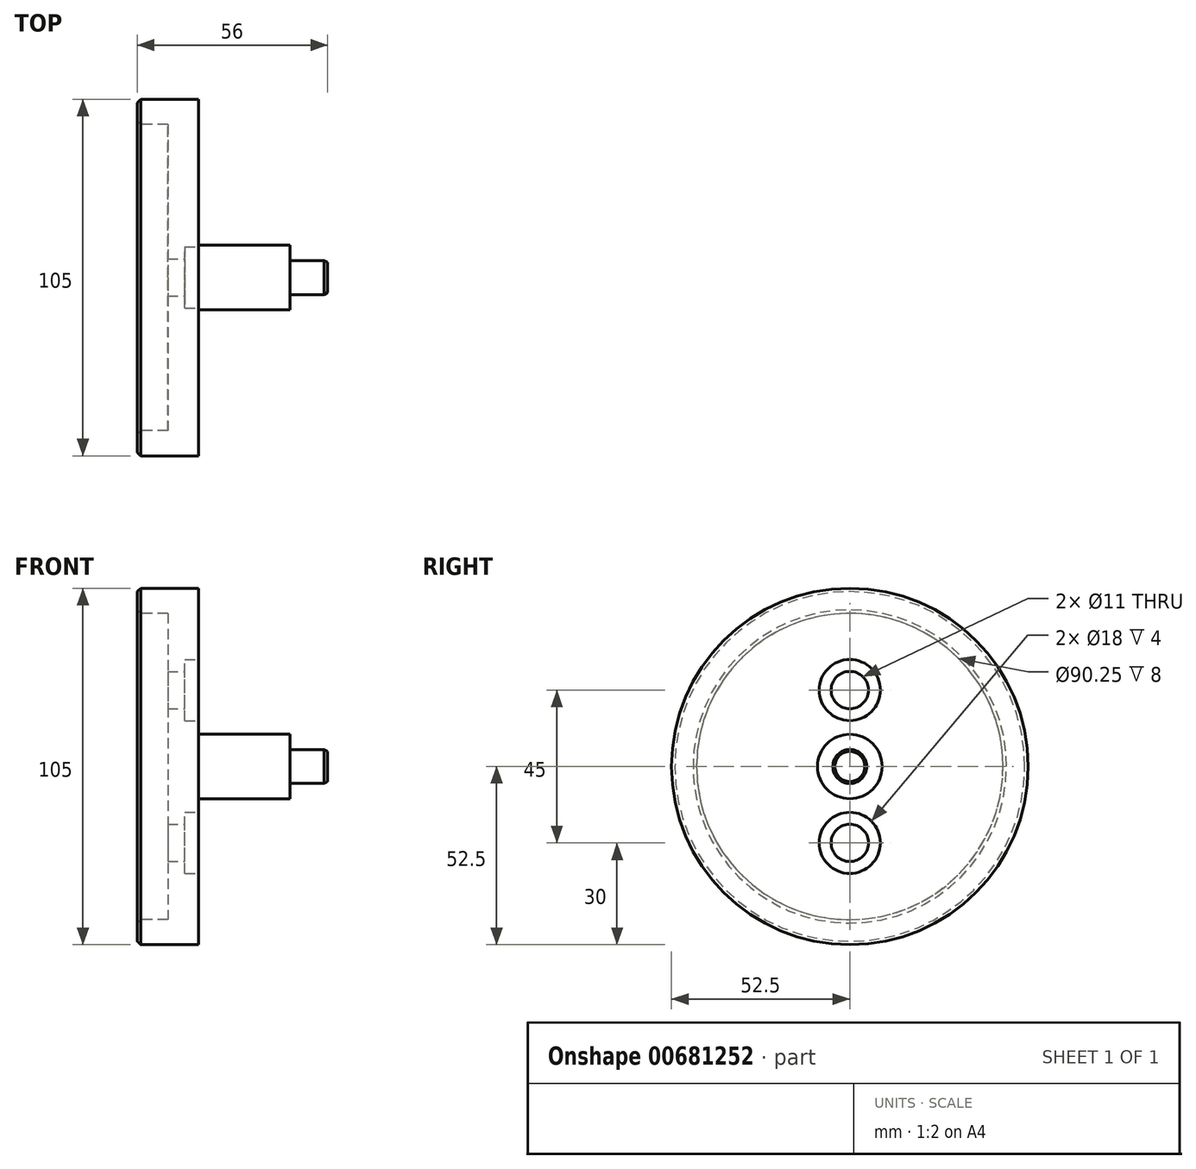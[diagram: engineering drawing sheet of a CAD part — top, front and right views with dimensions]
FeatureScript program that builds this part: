
annotation { "Feature Type Name" : "Feature", "Feature Type Description" : "" }
export const myFeature = defineFeature(function(context is Context, id is Id, definition is map)
    precondition{}
    {
        {
            var Q0;
            Q0=qCreatedBy(makeId("Right.planeOp"),FACE);
            var sketch = newSketch(context, id + "F0", { "sketchPlane" : qUnion([Q0])});
            skCircle(sketch, "E0", {"center": v(0, 0) * mm, "radius": 52.5 * mm});
            skSolve(sketch);
        }
        {
            var Q0;
            Q0=qSketchRegion(id+"F0",true);
            extrude(context, id + "F1", {"entities" : qUnion([Q0]), "oppositeDirection" : true, "depth" : (56 - 38) * mm, "offsetDistance" : 25 * mm});
        }
        {
            var Q0;
            Q0=makeQuery(id+"F1.opExtrude","CAP_FACE",FACE,{"disambiguationData":[OSD([sQuery(id+"F0.wireOp",EDGE,"E0")])],"isStart":false});
            var sketch = newSketch(context, id + "F2", { "sketchPlane" : qUnion([Q0])});
            skCircle(sketch, "E1", {"center": v(0, 0) * mm, "radius": 45.12 * mm});
            skSolve(sketch);
        }
        {
            var Q0;
            Q0=qSketchRegion(id+"F2",true);
            extrude(context, id + "F3", {"entities" : qUnion([Q0]), "operationType" : NewBodyOperationType.REMOVE, "oppositeDirection" : true, "depth" : 9 * mm, "offsetDistance" : 25 * mm});
        }
        {
            var Q0;
            Q0=makeQuery(id+"F1.opExtrude","CAP_FACE",FACE,{"disambiguationData":[OSD([sQuery(id+"F0.wireOp",EDGE,"E0")])],"isStart":false});
            chamfer(context, id + "F4", {"entities" : qUnion([Q0]), "width" : 1 * mm, "tangentPropagation" : true});
        }
        {
            var Q0;
            Q0=makeQuery(id+"F1.opExtrude","CAP_FACE",FACE,{"disambiguationData":[OSD([sQuery(id+"F0.wireOp",EDGE,"E0")])],"isStart":true});
            var sketch = newSketch(context, id + "F5", { "sketchPlane" : qUnion([Q0])});
            skCircle(sketch, "E2", {"center": v(0, 0) * mm, "radius": 9.5 * mm});
            skSolve(sketch);
        }
        {
            var Q0;
            Q0=qSketchRegion(id+"F5",true);
            extrude(context, id + "F6", {"entities" : qUnion([Q0]), "operationType" : NewBodyOperationType.ADD, "depth" : (38 - 11) * mm, "offsetDistance" : 25 * mm});
        }
        {
            var Q0;
            Q0=makeQuery(id+"F6.opExtrude","CAP_FACE",FACE,{"disambiguationData":[OSD([sQuery(id+"F5.wireOp",EDGE,"E2")])],"isStart":false});
            var sketch = newSketch(context, id + "F7", { "sketchPlane" : qUnion([Q0])});
            skCircle(sketch, "E3", {"center": v(0, 0) * mm, "radius": 5 * mm});
            skSolve(sketch);
        }
        {
            var Q0;
            Q0=qSketchRegion(id+"F7",true);
            extrude(context, id + "F8", {"entities" : qUnion([Q0]), "operationType" : NewBodyOperationType.ADD, "depth" : 11 * mm, "offsetDistance" : 25 * mm});
        }
        {
            var Q0;
            Q0=makeQuery(id+"F8.opExtrude","CAP_EDGE",EDGE,{"disambiguationData":[OSD([sQuery(id+"F7.wireOp",EDGE,"E3")])],"isStart":false});
            chamfer(context, id + "F9", {"entities" : qUnion([Q0]), "chamferType" : ChamferType.OFFSET_ANGLE, "width" : 1 * mm, "oppositeDirection" : true, "angle" : 30 * degree, "tangentPropagation" : true});
        }
        {
            var Q0;
            Q0=makeQuery(id+"F1.opExtrude","CAP_FACE",FACE,{"disambiguationData":[OSD([sQuery(id+"F0.wireOp",EDGE,"E0")])],"isStart":true});
            var sketch = newSketch(context, id + "F10", { "sketchPlane" : qUnion([Q0])});
            skLineSegment(sketch, "E4", {"start": v(0, -22.5) * mm, "end": v(0, 22.5) * mm, "construction": true});
            skPoint(sketch, "E5", {"position": v(0, -22.5) * mm});
            skPoint(sketch, "E6", {"position": v(0, 22.5) * mm});
            skSolve(sketch);
        }
        {
            var Q0;
            Q0=sQuery(id+"F10.wireOp",VERTEX,"E5");
            var Q1;
            Q1=sQuery(id+"F10.wireOp",VERTEX,"E6");
            var Q2;
            Q2=makeQuery(id+"F1.opExtrude","SWEPT_BODY",BODY,{"disambiguationData":[OSD([sQuery(id+"F0.wireOp",EDGE,"E0")])]});
            hole(context, id + "F11", {"style" : HoleStyle.C_BORE, "endStyle" : HoleEndStyle.THROUGH, "holeDiameter" : 11 * mm, "cBoreDiameter" : 18 * mm, "cBoreDepth" : 4 * mm, "majorDiameter" : 5 * mm, "isTappedThrough" : true, "tappedDepth" : 24.75 * mm, "tapClearance" : 3, "locations" : qUnion([Q0, Q1]), "scope" : qUnion([Q2])});
        }
    });
